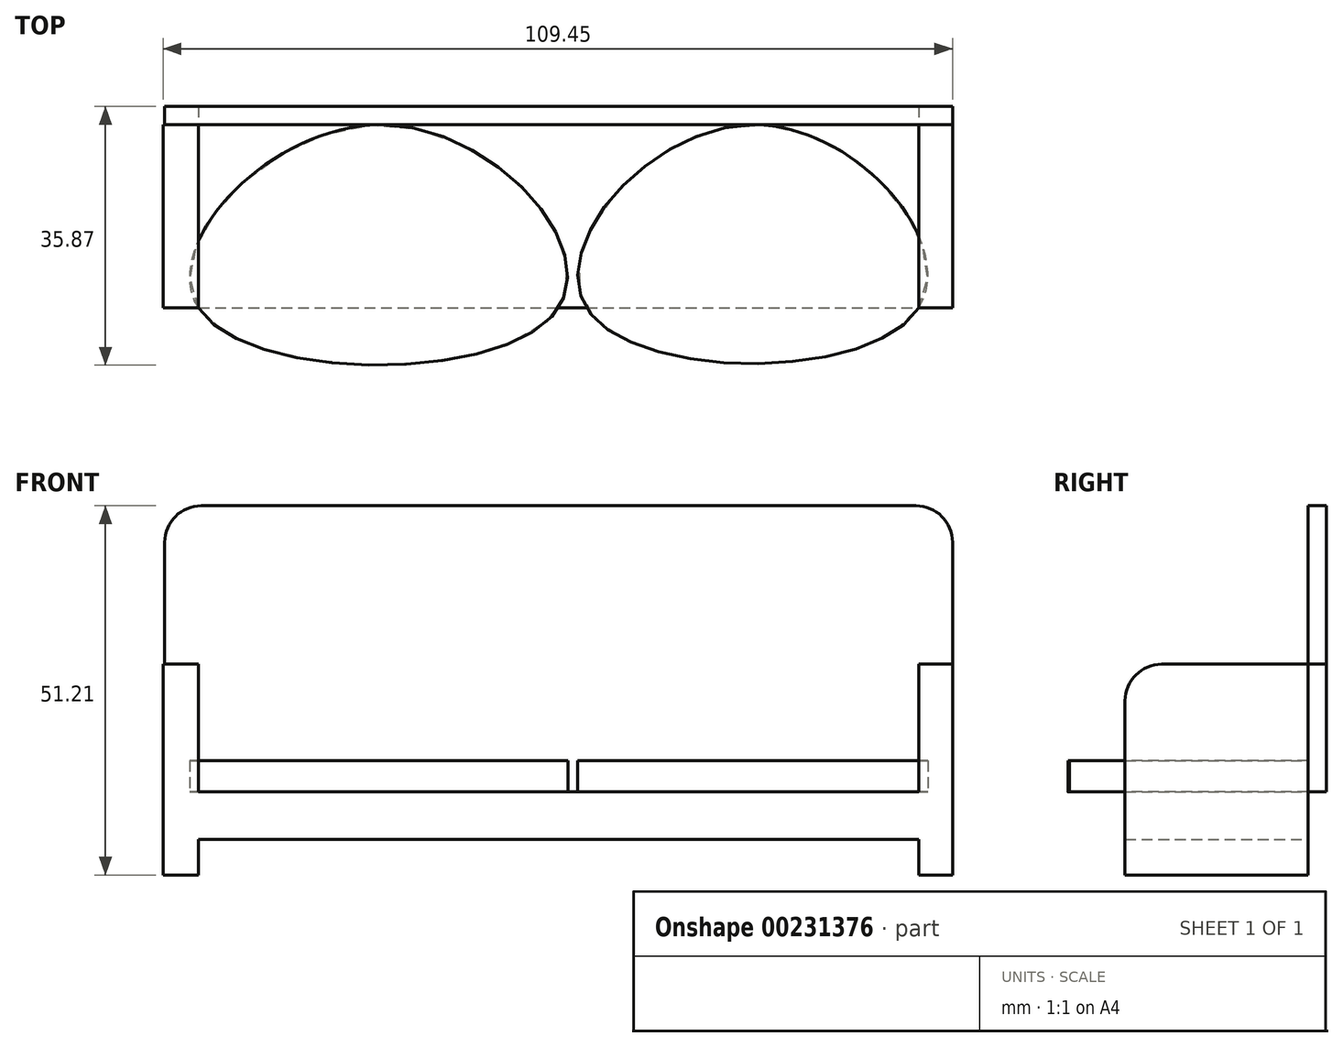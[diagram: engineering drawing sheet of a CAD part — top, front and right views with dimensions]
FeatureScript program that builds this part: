
annotation { "Feature Type Name" : "Feature", "Feature Type Description" : "" }
export const myFeature = defineFeature(function(context is Context, id is Id, definition is map)
    precondition{}
    {
        {
            var Q0;
            Q0=qCreatedBy(makeId("Front.planeOp"),FACE);
            var sketch = newSketch(context, id + "F0", { "sketchPlane" : qUnion([Q0])});
            skLineSegment(sketch, "E0.bottom", {"start": v(-51.63, -10.03) * mm, "end": v(48.22, -10.03) * mm});
            skLineSegment(sketch, "E0.top", {"start": v(-51.63, -3.41) * mm, "end": v(48.22, -3.41) * mm});
            skLineSegment(sketch, "E0.left", {"start": v(-51.63, -10.03) * mm, "end": v(-51.63, -3.41) * mm});
            skLineSegment(sketch, "E0.right", {"start": v(48.22, -10.03) * mm, "end": v(48.22, -3.41) * mm});
            skLineSegment(sketch, "E1.bottom", {"start": v(-51.63, 14.3) * mm, "end": v(-56.54, 14.3) * mm});
            skLineSegment(sketch, "E1.top", {"start": v(-51.63, -14.94) * mm, "end": v(-56.54, -14.94) * mm});
            skLineSegment(sketch, "E1.left", {"start": v(-51.63, 14.3) * mm, "end": v(-51.63, -14.94) * mm});
            skLineSegment(sketch, "E1.right", {"start": v(-56.54, 14.3) * mm, "end": v(-56.54, -14.94) * mm});
            skLineSegment(sketch, "E2.bottom", {"start": v(48.22, 14.3) * mm, "end": v(52.91, 14.3) * mm});
            skLineSegment(sketch, "E2.top", {"start": v(48.22, -14.94) * mm, "end": v(52.91, -14.94) * mm});
            skLineSegment(sketch, "E2.left", {"start": v(48.22, 14.3) * mm, "end": v(48.22, -14.94) * mm});
            skLineSegment(sketch, "E2.right", {"start": v(52.91, 14.3) * mm, "end": v(52.91, -14.94) * mm});
            skSolve(sketch);
        }
        {
            var Q0;
            {var subQ3=sQuery(id+"F0.wireOp",EDGE,"E1.bottom");Q0=makeQuery(id+"F0.imprint","IMPRINT",FACE,{"disambiguationData":[TD([[makeQuery(id+"F0.imprint","IMPRINT",EDGE,{"derivedFrom":subQ3}),1.0]])]});}
            var sketch = newSketch(context, id + "F1", { "sketchPlane" : qUnion([Q0])});
            skSolve(sketch);
        }
        {
            var Q0;
            Q0 = qSketchRegion(id + "F1", true);
            var Q1;
            {var subQ3=sQuery(id+"F0.wireOp",EDGE,"E2.bottom");Q1=makeQuery(id+"F0.imprint","IMPRINT",FACE,{"disambiguationData":[TD([[makeQuery(id+"F0.imprint","IMPRINT",EDGE,{"derivedFrom":subQ3}),-1.0]])]});}
            var Q2;
            {var subQ0=sQuery(id+"F0.wireOp",EDGE,"E0.bottom");Q2=makeQuery(id+"F0.imprint","IMPRINT",FACE,{"disambiguationData":[TD([[makeQuery(id+"F0.imprint","IMPRINT",EDGE,{"derivedFrom":subQ0}),1.0]])]});}
            var Q3;
            {var subQ3=sQuery(id+"F0.wireOp",EDGE,"E1.bottom");Q3=makeQuery(id+"F0.imprint","IMPRINT",FACE,{"disambiguationData":[TD([[makeQuery(id+"F0.imprint","IMPRINT",EDGE,{"derivedFrom":subQ3}),1.0]])]});}
            extrude(context, id + "F2", {"entities" : qUnion([Q0, Q1, Q2, Q3]), "depth" : 25.4 * mm});
        }
        {
            var Q0;
            Q0=makeQuery(id+"F2.opExtrude","CAP_FACE",FACE,{"disambiguationData":[OSD([sQuery(id+"F0.wireOp",EDGE,"E0.bottom"),sQuery(id+"F0.wireOp",EDGE,"E0.top"),sQuery(id+"F0.wireOp",EDGE,"E1.bottom"),sQuery(id+"F0.wireOp",EDGE,"E1.top"),sQuery(id+"F0.wireOp",EDGE,"E1.left"),sQuery(id+"F0.wireOp",EDGE,"E1.right"),sQuery(id+"F0.wireOp",EDGE,"E2.bottom"),sQuery(id+"F0.wireOp",EDGE,"E2.top"),sQuery(id+"F0.wireOp",EDGE,"E2.left"),sQuery(id+"F0.wireOp",EDGE,"E2.right")])],"isStart":true});
            var sketch = newSketch(context, id + "F3", { "sketchPlane" : qUnion([Q0])});
            skLineSegment(sketch, "E3.bottom", {"start": v(-52.91, -8.96) * mm, "end": v(56.33, -8.96) * mm});
            skLineSegment(sketch, "E3.top", {"start": v(-52.91, 36.27) * mm, "end": v(56.33, 36.27) * mm});
            skLineSegment(sketch, "E3.left", {"start": v(-52.91, -8.96) * mm, "end": v(-52.91, 36.27) * mm});
            skLineSegment(sketch, "E3.right", {"start": v(56.33, -8.96) * mm, "end": v(56.33, 36.27) * mm});
            skSolve(sketch);
        }
        {
            var Q0;
            {var subQ4=sQuery(id+"F3.wireOp",EDGE,"E3.top");Q0=makeQuery(id+"F3.imprint","IMPRINT",FACE,{"disambiguationData":[TD([[makeQuery(id+"F3.imprint","IMPRINT",EDGE,{"derivedFrom":subQ4}),-1.0]])]});}
            var sketch = newSketch(context, id + "F4", { "sketchPlane" : qUnion([Q0])});
            skSolve(sketch);
        }
        {
            var Q0;
            Q0 = qSketchRegion(id + "F4", true);
            var Q1;
            {var subQ4=sQuery(id+"F3.wireOp",EDGE,"E3.top");Q1=makeQuery(id+"F3.imprint","IMPRINT",FACE,{"disambiguationData":[TD([[makeQuery(id+"F3.imprint","IMPRINT",EDGE,{"derivedFrom":subQ4}),-1.0]])]});}
            extrude(context, id + "F5", {"entities" : qUnion([Q0, Q1]), "depth" : 2.54 * mm});
        }
        {
            var Q0;
            Q0=makeQuery(id+"F5.opExtrude","SWEPT_EDGE",EDGE,{"disambiguationData":[OSD([sQuery(id+"F3.wireOp",EDGE,"E3.top"),sQuery(id+"F3.wireOp",EDGE,"E3.right")])]});
            fillet(context, id + "F6", {"entities" : qUnion([Q0]), "radius" : 5.08 * mm, "tangentPropagation" : true, "allowEdgeOverflow" : false});
        }
        {
            var Q0;
            Q0=makeQuery(id+"F5.opExtrude","SWEPT_EDGE",EDGE,{"disambiguationData":[OSD([sQuery(id+"F3.wireOp",EDGE,"E3.top"),sQuery(id+"F3.wireOp",EDGE,"E3.left")])]});
            fillet(context, id + "F7", {"entities" : qUnion([Q0]), "radius" : 5.08 * mm, "tangentPropagation" : true, "allowEdgeOverflow" : false});
        }
        {
            var Q0;
            Q0=makeQuery(id+"F2.opExtrude","CAP_EDGE",EDGE,{"disambiguationData":[OSD([sQuery(id+"F0.wireOp",EDGE,"E1.bottom")])],"isStart":false});
            fillet(context, id + "F8", {"entities" : qUnion([Q0]), "radius" : 5.08 * mm, "tangentPropagation" : true, "allowEdgeOverflow" : false});
        }
        {
            var Q0;
            Q0=makeQuery(id+"F2.opExtrude","CAP_EDGE",EDGE,{"disambiguationData":[OSD([sQuery(id+"F0.wireOp",EDGE,"E2.bottom")])],"isStart":false});
            fillet(context, id + "F9", {"entities" : qUnion([Q0]), "radius" : 5.08 * mm, "tangentPropagation" : true, "allowEdgeOverflow" : false});
        }
        {
            var Q0;
            Q0=makeQuery(id+"F2.opExtrude","SWEPT_FACE",FACE,{"disambiguationData":[OSD([sQuery(id+"F0.wireOp",EDGE,"E0.top")])]});
            var sketch = newSketch(context, id + "F10", { "sketchPlane" : qUnion([Q0])});
            skFitSpline(sketch, "E4", {"points": [v(-51.63, -25.4) * mm, v(-26.24, 0) * mm, v(-1.7, -25.4) * mm, v(-51.63, -25.4) * mm]});
            skFitSpline(sketch, "E5", {"points": [v(48.22, -25.4) * mm, v(25.48, 0) * mm, v(2.14, -25.4) * mm, v(48.22, -25.4) * mm]});
            skSolve(sketch);
        }
        {
            var Q0;
            Q0 = qSketchRegion(id + "F10", true);
            extrude(context, id + "F11", {"entities" : qUnion([Q0]), "depth" : 4.32 * mm});
        }
    });
